# Revit family: Trane_TVR_Indoor_Wall mounted_4TVW0024(27,30)EF000AA(2nd DC)
name_source: partatom
category: Equipamento mecânico
units: mm (PartAtom-declared; Revit-internal decimal feet)

## family parameters
Com base no plano de trabalho = Não
Compartilhado = Não
Corte com vazios quando carregada = Não
Cota do conector redondo = Utilizar diâmetro
Número OmniClass = 23.75.00.00
Ponto de cálculo do ambiente = Não
Sempre na vertical = Sim
Tipo de parte = Normal
Título OmniClass = Climate Control (HVAC)

## types (3) — shared parameters
Condensation = air
Depth = 262  [stored 0.85958 ft]
Descrição = High efficiency air cooled
Fabricante = Trane
Gas = R410a
Gas pipe = 15.9  [stored 0.0521654 ft]
Height = 343  [stored 1.12533 ft]
Installation = Indoor installation
Liquid pipe = 9.53
Machine material = Galvanized Steel
Maximum Fuse Amps = 15 A
Minimum Circuit Amps = 1 A
Net Weight = 17.00 kg
Panel color = S1022
Power supply = 220-240V ~50/60Hz
Series = TVR ULTRA
URL = https://www.trane.com
Width = 1194
zero-valued in all types: clearance access behind, clearance access front, clearance access left, clearance access right

## per-type parameters (varying)
| type | Air  Flow | Cooling Capacity | Cooling Power Input | Heating Capacity | Heating Power Input |
| 4TVW0024EF000AA | 1195/1130/1065/1005/940/875/809 m3/h | 7 kW | 55 W | 8 kW | 55 W |
| 4TVW0027EF000AA | 1195/1130/1065/1005/940/875/809 m3/h | 8 kW | 55 W | 9 kW | 55 W |
| 4TVW0030EF000AA | 1421/1300/1125/1067/1005/934/867 m3/h | 9 kW | 82 W | 10 kW | 82 W |

note: column(s) folded — value = type name in every type: Modelo

note: [stored X ft] marks values corroborated as IEEE doubles in the binary element streams (Revit-internal decimal feet)
